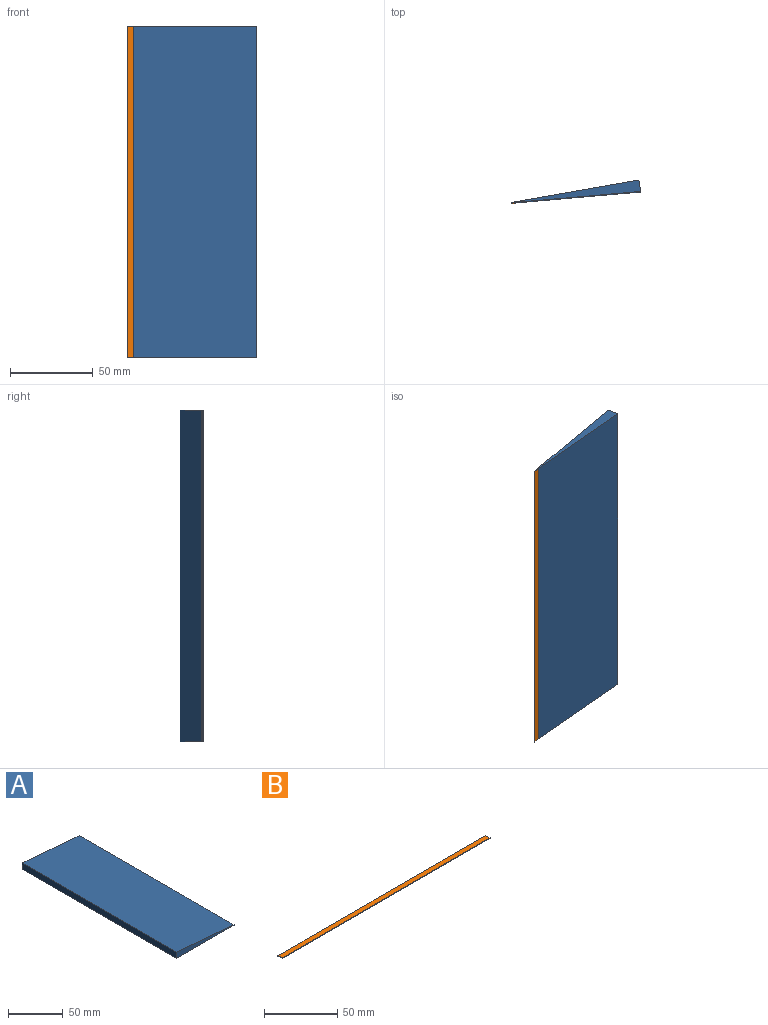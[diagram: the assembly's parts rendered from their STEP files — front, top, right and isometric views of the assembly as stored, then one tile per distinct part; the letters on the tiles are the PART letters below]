
ASSEMBLY  parts=2 mates=1
PART A: 6 faces, bbox 74.3x200x7 mm
  f0: plane 200x74.29mm, normal (0,0,-1), area 14857mm2, adj f1,f3,f4,f5
  f1: plane 200x0.5mm, normal (1,0,0), area 100mm2, adj f0,f2,f4,f5
  f2: plane 200x74.29mm, normal (0.09,0,1), area 14913.7mm2, adj f1,f3,f4,f5
  f3: plane 200x7mm, normal (-1,0,0), area 1399.8mm2, adj f0,f2,f4,f5
  f4: plane 74.29x7mm, normal (0,-1,0), area 278.5mm2, adj f0,f1,f2,f3
  f5: plane 74.29x7mm, normal (0,1,0), area 278.5mm2, adj f0,f1,f2,f3
PART B: 6 faces, bbox 200x4x0.5 mm
  f0: plane 200x4mm, normal (0,0,1), area 800mm2, adj f1,f3,f4,f5
  f1: plane 4x0.5mm, normal (-1,0,0), area 2mm2, adj f0,f2,f4,f5
  f2: plane 200x4mm, normal (0,0,-1), area 800mm2, adj f1,f3,f4,f5
  f3: plane 4x0.5mm, normal (1,0,0), area 2mm2, adj f0,f2,f4,f5
  f4: plane 200x0.5mm, normal (0,-1,0), area 100mm2, adj f0,f1,f2,f3
  f5: plane 200x0.5mm, normal (0,1,0), area 100mm2, adj f0,f1,f2,f3
PLACE A rot(axis=(-0.06,0.71,-0.71),172.9deg) t=(-161.89,60.75,-195.87)mm
PLACE B rot(axis=(-0.61,0.51,0.61),125.9deg) t=(16.42,128.1,-96.27)mm
MATE fastened A.f1 <-> B.f4  axis (-0.98,-0.17,0) through (26.54,93.72,-95.87)mm
